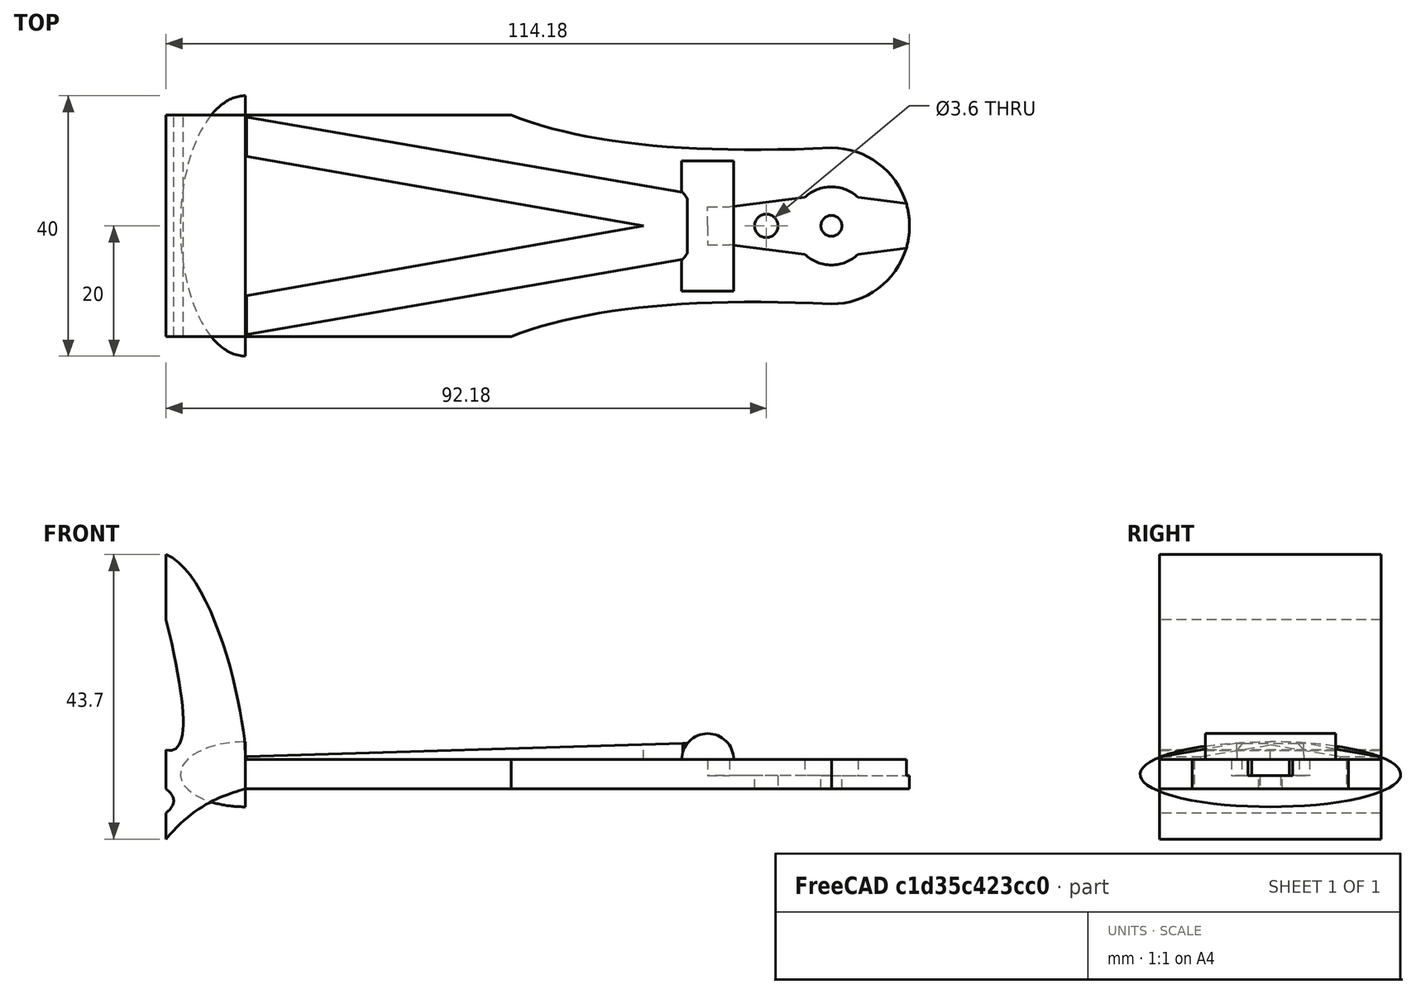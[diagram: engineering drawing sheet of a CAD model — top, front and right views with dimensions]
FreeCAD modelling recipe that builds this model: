
FCSTD DOCUMENT  (FreeCAD 0.18.4R)
Label: ServoCrawlerLeg
License: All rights reserved
LicenseURL: http://en.wikipedia.org/wiki/All_rights_reserved
objects: TechDraw::DrawViewDimension×8, Sketcher::SketchObject×7, TechDraw::DrawViewPart×7, Part::Extrusion×5, Part::MultiFuse×3, Part::Mirroring×2, Part::Cut×2, TechDraw::DrawSVGTemplate×2, TechDraw::DrawViewAnnotation×2, TechDraw::DrawPage×2, Spreadsheet::Sheet×1, Part::Fuse×1, Part::Ellipsoid×1, PartDesign::FeatureBase×1, PartDesign::Pad×1, PartDesign::Pocket×1, PartDesign::Body×1
note: 27 computed .brp shape members not serialized (recipe doc carries the construction recipe); baked Part::Feature solids carry a one-line shape summary decoded from their .brp

FEATURE [Sketcher::SketchObject] Sketch001
  sketch-geometry (15):
    g0: GeomPoint X=-90 Y=17 Z=0
    g1: LineSegment StartX=-90 StartY=17 StartZ=0 EndX=-49.2057 EndY=17 EndZ=0
    g2: Circle [constr] CenterX=0 CenterY=12 CenterZ=0 NormalX=0 NormalY=0 NormalZ=1 AngleXU=0 Radius=6
    g3: Circle [constr] CenterX=-49.2057 CenterY=17 CenterZ=0 NormalX=0 NormalY=0 NormalZ=1 AngleXU=0 Radius=6
    g4: ArcOfCircle CenterX=0 CenterY=0 CenterZ=0 NormalX=0 NormalY=0 NormalZ=1 AngleXU=0 Radius=12 StartAngle=0 EndAngle=1.5708
    g5: ArcOfCircle CenterX=0 CenterY=0 CenterZ=0 NormalX=0 NormalY=0 NormalZ=1 AngleXU=0 Radius=1.6 StartAngle=0 EndAngle=3.14159
    g6: LineSegment StartX=1.6 StartY=0 StartZ=0 EndX=12 EndY=0 EndZ=0
    g7: LineSegment StartX=-1.6 StartY=0 StartZ=0 EndX=-90 EndY=0 EndZ=0
    g8: Circle [constr] CenterX=0 CenterY=12 CenterZ=0 NormalX=0 NormalY=0 NormalZ=1 AngleXU=0 Radius=5
    g9: Circle [constr] CenterX=-32.5091 CenterY=10.4213 CenterZ=0 NormalX=0 NormalY=0 NormalZ=1 AngleXU=0 Radius=5
    g10: Circle [constr] CenterX=-49.2057 CenterY=17 CenterZ=0 NormalX=0 NormalY=0 NormalZ=1 AngleXU=0 Radius=5
    g11: BSplineCurve PolesCount=3 KnotsCount=2 Degree=2 IsPeriodic=0
    g12: GeomPoint [constr] X=0 Y=12 Z=0
    g13: GeomPoint [constr] X=-49.2057 Y=17 Z=0
    g14: LineSegment StartX=-90 StartY=0 StartZ=0 EndX=-90 EndY=17 EndZ=0
  constraints (28):
    c: DistanceX(g0,g2) = 90  'length'
    c: DistanceY(g2,g0) = 5
    c: Coincident(g1,g0)
    c: Horizontal(g1)
    c: Radius(g2) = 6
    c: Equal(g2,g3)
    c: Coincident(g3,g1)
    c: PointOnObject(g4,g-1)
    c: PointOnObject(g7,g-1)
    c: Coincident(g5,g-1)
    c: PointOnObject(g5,g-1)
    c: Coincident(g6,g5)
    c: Coincident(g6,g4)
    c: Horizontal(g6)
    c: Coincident(g7,g5)
    c: Radius(g5) = 1.6
    c: Radius(g8) = 5
    c: Equal(g8,g9)
    c: Equal(g8,g10)
    c: Coincident(g10,g1)
    c: InternalAlignment(g8,g11)
    c: InternalAlignment(g9,g11)
    c: InternalAlignment(g10,g11)
    c: InternalAlignment(g12,g11)
    c: InternalAlignment(g13,g11)
    c: Coincident(g14,g0)
    c: Coincident(g14,g7)
    c: Coincident(g8,g2)
FEATURE [Part::Extrusion] Extrude  label="arm"
  Base = -> Sketch001
  Dir = (0,0,1)
  DirMode = 2
  FaceMakerClass = Part::FaceMakerBullseye
  LengthFwd = 4.5
  LengthRev = 0
  Solid = true
  Symmetric = false
  expr: LengthFwd = global.height
FEATURE [Sketcher::SketchObject] Sketch008  label="servoHolderHole"
  AttachmentOffset = pos=(0,0,0) rot=(0,0,1;1.5708rad)
  MapMode = 5
  Placement = pos=(0,0,4.5) rot=(0,0,1;1.5708rad)
  Support = -> [Extrude]
  sketch-geometry (7):
    g0: GeomPoint X=0 Y=19 Z=0
    g1: LineSegment StartX=0 StartY=19 StartZ=0 EndX=2.9 EndY=19 EndZ=0
    g2: LineSegment StartX=2.9 StartY=19 StartZ=0 EndX=2.9 EndY=15.6827 EndZ=0
    g3: ArcOfCircle CenterX=0 CenterY=0 CenterZ=0 NormalX=0 NormalY=0 NormalZ=1 AngleXU=0 Radius=6 StartAngle=0 EndAngle=0.747584
    g4: LineSegment StartX=4.4 StartY=4.07922 StartZ=0 EndX=2.9 EndY=15.6827 EndZ=0
    g5: LineSegment StartX=0 StartY=0 StartZ=0 EndX=6 EndY=0 EndZ=0
    g6: LineSegment StartX=0 StartY=0 StartZ=0 EndX=0 EndY=19 EndZ=0
  constraints (18):
    c: PointOnObject(g0,g-2)
    c: DistanceY(g-1,g0) = 19  'servHoleL'
    c: Coincident(g1,g0)
    c: Horizontal(g1)
    c: DistanceX(g1,g1) = 2.9
    c: Coincident(g2,g1)
    c: Vertical(g2)
    c: Coincident(g3,g-1)
    c: Radius(g3) = 6
    c: PointOnObject(g3,g-1)
    c: DistanceX(g-1,g3) = 4.4
    c: Coincident(g4,g2)
    c: Distance(g4) = 11.7
    c: Coincident(g4,g3)
    c: Coincident(g5,g-1)
    c: Coincident(g5,g3)
    c: Coincident(g6,g-1)
    c: Coincident(g6,g0)
FEATURE [Spreadsheet::Sheet] Spreadsheet  label="global"
  cells = A1=height; B1(height)=4.5; A2=offsetBackwardServo; B2(offestSev)=-2.5
FEATURE [Part::Extrusion] Extrude004
  Base = -> Sketch008
  Dir = (0,0,1)
  DirMode = 2
  FaceMakerClass = Part::FaceMakerBullseye
  LengthFwd = 2.45
  LengthRev = 0
  Reversed = true
  Solid = true
  Symmetric = false
FEATURE [Part::Mirroring] Part__Mirroring002  label="Extrude004 (Mirror #3)"
  Base = (0,0,0)
  Normal = (1,0,0)
  Source = -> Extrude004
FEATURE [Part::MultiFuse] Fusion003
  Shapes = -> [Part__Mirroring002,Extrude004]
FEATURE [Part::Cut] Cut
  Base = -> Extrude
  Tool = -> Fusion003
FEATURE [Part::Mirroring] Part__Mirroring  label="Extrude (Mirror #1)"
  Base = (0,0,0)
  Normal = (0,1,0)
  Source = -> Cut
FEATURE [Sketcher::SketchObject] Sketch012
  MapMode = 5
  Placement = pos=(0,0,4) rot=(0,0,1;0rad)
  sketch-geometry (9):
    g0: LineSegment StartX=-89.8501 StartY=16.7026 StartZ=0 EndX=-22.8408 EndY=5.14242 EndZ=0
    g1: LineSegment StartX=-22.8408 StartY=-5.14242 StartZ=0 EndX=-89.8501 EndY=-16.7026 EndZ=0
    g2: LineSegment StartX=-89.8501 StartY=-16.7026 StartZ=0 EndX=-89.8501 EndY=-10.7026 EndZ=0
    g3: LineSegment StartX=-89.8501 StartY=-10.7026 StartZ=0 EndX=-28.8408 EndY=0 EndZ=0
    g4: LineSegment StartX=-28.8408 StartY=0 StartZ=0 EndX=-89.8501 EndY=10.7026 EndZ=0
    g5: LineSegment StartX=-89.8501 StartY=10.7026 StartZ=0 EndX=-89.8501 EndY=16.7026 EndZ=0
    g6: ArcOfCircle CenterX=-28.8408 CenterY=0 CenterZ=0 NormalX=0 NormalY=0 NormalZ=1 AngleXU=0 Radius=7.90218 StartAngle=5.5746 EndAngle=6.99177
    g7: LineSegment [constr] StartX=-89.8501 StartY=10.7026 StartZ=0 EndX=-89.8501 EndY=0 EndZ=0
    g8: LineSegment [constr] StartX=-89.8501 StartY=0 StartZ=0 EndX=-89.8501 EndY=-10.7026 EndZ=0
  constraints (22):
    c: Coincident(g2,g1)
    c: Vertical(g2)
    c: Coincident(g3,g2)
    c: PointOnObject(g3,g-1)
    c: Coincident(g4,g3)
    c: Coincident(g5,g4)
    c: Coincident(g5,g0)
    c: Vertical(g5)
    c: DistanceY(g2,g2) = 6
    c: DistanceY(g5,g5) = 6
    c: Coincident(g6,g3)
    c: Coincident(g6,g0)
    c: Coincident(g6,g1)
    c: DistanceX(g3,g0) = 6
    c: DistanceX(g3,g1) = 6
    c: Coincident(g7,g4)
    c: PointOnObject(g7,g-1)
    c: Coincident(g8,g7)
    c: Coincident(g8,g2)
    c: Vertical(g7)
    c: Vertical(g8)
    c: Equal(g7,g8)
FEATURE [Sketcher::SketchObject] Sketch013
  MapMode = 5
  Placement = pos=(0,0,0) rot=(1,0,0;1.5708rad)
  sketch-geometry (3):
    g0: LineSegment StartX=-90 StartY=5 StartZ=0 EndX=-22.1184 EndY=7 EndZ=0
    g1: LineSegment StartX=-22.1184 StartY=7 StartZ=0 EndX=-90 EndY=7 EndZ=0
    g2: LineSegment StartX=-90 StartY=7 StartZ=0 EndX=-90 EndY=5 EndZ=0
  constraints (8):
    c: Coincident(g1,g0)
    c: Horizontal(g1)
    c: Coincident(g2,g1)
    c: Coincident(g2,g0)
    c: Vertical(g2)
    c: DistanceX(g0,g-1) = 90
    c: DistanceY(g-1,g0) = 7
    c: DistanceY(g0,g1) = 2
FEATURE [Part::Extrusion] Extrude005
  Base = -> Sketch012
  Dir = (0,0,1)
  DirMode = 2
  FaceMakerClass = Part::FaceMakerBullseye
  LengthFwd = 3
  LengthRev = 0
  Solid = true
  Symmetric = false
FEATURE [Part::Extrusion] Extrude006
  Base = -> Sketch013
  Dir = (0,-1,0)
  DirMode = 2
  FaceMakerClass = Part::FaceMakerBullseye
  LengthFwd = 30
  LengthRev = 30
  Solid = true
  Symmetric = false
FEATURE [Part::Cut] Cut001  label="Strebe"
  Base = -> Extrude005
  Tool = -> Extrude006
FEATURE [Part::Fuse] Fusion
  Base = -> Cut
  Tool = -> Part__Mirroring
FEATURE [TechDraw::DrawSVGTemplate] Template
  EditableTexts = Designed_by_Name=Johannes Löwe; Drawing_number=0.0.1; FC-Date=24/03/2019; FC-SC=-; FC-SH=1; FC-Title=S.L.A.R Leg; Subtitle=Middle Component; Weight=19.5 g
  Height = 210
  Orientation = 1
  Width = 297
FEATURE [TechDraw::DrawViewPart] View  label="Top"
  Caption = Top
  CoarseView = true
  Direction = (0,0,1)
  Focus = 100
  HardHidden = false
  IsoCount = 0
  IsoHidden = false
  IsoVisible = true
  LockPosition = false
  Perspective = false
  Rotation = 0
  ScaleType = 1
  SeamHidden = false
  SeamVisible = false
  SmoothHidden = false
  SmoothVisible = true
  X = 133.52
  Y = 56.71
FEATURE [TechDraw::DrawViewPart] View001  label="Front"
  Caption = Front
  CoarseView = true
  Direction = (0,1,0)
  Focus = 100
  HardHidden = false
  IsoCount = 0
  IsoHidden = false
  IsoVisible = false
  LockPosition = false
  Perspective = true
  Rotation = 0
  ScaleType = 0
  SeamHidden = false
  SeamVisible = false
  SmoothHidden = false
  SmoothVisible = false
  X = 216.314
  Y = 87.8478
FEATURE [TechDraw::DrawViewPart] View002  label="Perspective"
  Caption = The S.L.A.R. Leg
  CoarseView = true
  Direction = (-0.2,1,1)
  Focus = 200
  HardHidden = false
  IsoCount = 0
  IsoHidden = false
  IsoVisible = true
  LockPosition = false
  Perspective = false
  Rotation = 0
  Scale = 1.5
  ScaleType = 0
  SeamHidden = false
  SeamVisible = false
  SmoothHidden = true
  SmoothVisible = false
  X = 69.0301
  Y = 169.689
  expr: Direction.x = -0.2
FEATURE [TechDraw::DrawViewDimension] Dimension
  Arbitrary = false
  FormatSpec = %.2f
  LockPosition = false
  MeasureType = 1
  OverTolerance = 0
  References2D = -> [View]
  Rotation = 0
  ScaleType = 0
  Type = 2
  UnderTolerance = 0
  X = -113.183
  Y = -28.0041
FEATURE [TechDraw::DrawViewDimension] Dimension001
  Arbitrary = false
  FormatSpec = %.2f
  LockPosition = false
  MeasureType = 1
  OverTolerance = 0
  References2D = -> [View001]
  Rotation = 0
  ScaleType = 0
  Type = 1
  UnderTolerance = 0
  X = 31.1719
  Y = 20.5356
FEATURE [TechDraw::DrawViewDimension] Dimension002
  Arbitrary = false
  FormatSpec = %.2f
  LockPosition = false
  MeasureType = 1
  OverTolerance = 0
  References2D = -> [View]
  Rotation = 0
  ScaleType = 0
  Type = 2
  UnderTolerance = 0
  X = -69.0862
  Y = -0.822454
FEATURE [TechDraw::DrawViewDimension] Dimension003
  Arbitrary = false
  FormatSpec = %.2f
  LockPosition = false
  MeasureType = 1
  OverTolerance = 0
  References2D = -> [View]
  Rotation = 0
  ScaleType = 0
  Type = 2
  UnderTolerance = 0
  X = -91.294
  Y = -1.64851
FEATURE [TechDraw::DrawViewDimension] Dimension004
  Arbitrary = false
  FormatSpec = %.2f
  LockPosition = false
  MeasureType = 1
  OverTolerance = 0
  References2D = -> [View002]
  Rotation = 0
  ScaleType = 0
  Type = 0
  UnderTolerance = 0
  X = 1.50159
  Y = -39.0413
FEATURE [TechDraw::DrawViewAnnotation] Annotation
  Font = osifont
  LineSpace = 80
  LockPosition = false
  MaxWidth = -1
  Rotation = 0
  ScaleType = 0
  Text = Radboud University
  TextSize = 5
  TextStyle = 2
  X = 214.014
  Y = 35.8125
FEATURE [TechDraw::DrawPage] Page
  KeepUpdated = true
  ProjectionType = 0
  Template = -> Template
  Views = -> [View,View001,View002,Dimension,Dimension001,Dimension002,Dimension003,Dimension004,Annotation]
FEATURE [Part::MultiFuse] Fusion004
  Shapes = -> [Cut001,Fusion]
FEATURE [Sketcher::SketchObject] Sketch015  label="HoleServoScrew2"
  MapMode = 5
  Placement = pos=(0,0,4) rot=(0,0,1;0rad)
  sketch-geometry (1):
    g0: Circle CenterX=-10 CenterY=0 CenterZ=0 NormalX=0 NormalY=0 NormalZ=1 AngleXU=0 Radius=1.8
  constraints (3):
    c: PointOnObject(g0,g-1)
    c: DistanceX(g0,g-1) = 10
    c: Radius(g0) = 1.8
FEATURE [Part::Ellipsoid] Ellipsoid
  Angle1 = -90
  Angle2 = 90
  Angle3 = 180
  AttacherType = Attacher::AttachEngine3D
  Placement = pos=(-90,0,2.25) rot=(0,0,1;1.5708rad)
  Radius1 = 5
  Radius2 = 20
  Radius3 = 10
  expr: Placement.Base.z = global.height / 2
  expr: Placement.Base.x = -1 * Sketch001.Constraints.length
FEATURE [Sketcher::SketchObject] Sketch  label="shoe"
  Placement = pos=(0,0,0) rot=(1,0,0;1.5708rad)
  expr: Constraints[4] = arm.LengthFwd
  expr: Constraints[6] = servoHolderHole.Constraints.servHoleL
  sketch-geometry (2):
    g0: ArcOfCircle CenterX=-19 CenterY=4.5 CenterZ=0 NormalX=0 NormalY=0 NormalZ=1 AngleXU=0 Radius=4 StartAngle=0 EndAngle=3.14159
    g1: LineSegment StartX=-23 StartY=4.5 StartZ=0 EndX=-15 EndY=4.5 EndZ=0
  constraints (7):
    c: Radius(g0) = 4
    c: Coincident(g1,g0)
    c: Coincident(g1,g0)
    c: Horizontal(g1)
    c: DistanceY(g-1,g0) = 4.5
    c: PointOnObject(g0,g1)
    c: DistanceX(g0,g-1) = 19
FEATURE [Sketcher::SketchObject] Sketch016  label="Foot"
  Placement = pos=(0,0,0) rot=(1,0,0;1.5708rad)
  sketch-geometry (32):
    g0-g3: Circle [constr] x4 (B-spline internal-alignment scaffolding for g4; pole/knot coordinates omitted)
    g4: BSplineCurve PolesCount=4 KnotsCount=2 Degree=3 IsPeriodic=0
    g5: GeomPoint [constr] X=-90 Y=0 Z=0
    g6: GeomPoint [constr] X=-102.176 Y=-7.69826 Z=0
    g7: LineSegment StartX=-102.176 StartY=-7.69826 StartZ=0 EndX=-102.176 EndY=-3.69826 EndZ=0
    g8: Circle [constr] CenterX=-102.176 CenterY=-3.69826 CenterZ=0 NormalX=0 NormalY=0 NormalZ=1 AngleXU=0 Radius=0.9
    g9: Circle [constr] CenterX=-99.8759 CenterY=-1.76634 CenterZ=0 NormalX=0 NormalY=0 NormalZ=1 AngleXU=0 Radius=0.9
    g10: Circle [constr] CenterX=-102.176 CenterY=0 CenterZ=0 NormalX=0 NormalY=0 NormalZ=1 AngleXU=0 Radius=0.9
    g11: BSplineCurve PolesCount=3 KnotsCount=2 Degree=2 IsPeriodic=0
    g12: GeomPoint [constr] X=-102.176 Y=-3.69826 Z=0
    g13: GeomPoint [constr] X=-102.176 Y=0 Z=0
    g14: LineSegment StartX=-102.176 StartY=0 StartZ=0 EndX=-102.176 EndY=6 EndZ=0
    g15: Circle [constr] CenterX=-102.176 CenterY=6 CenterZ=0 NormalX=0 NormalY=0 NormalZ=1 AngleXU=0 Radius=0.8
    g16: Circle [constr] CenterX=-96.9441 CenterY=4.63827 CenterZ=0 NormalX=0 NormalY=0 NormalZ=1 AngleXU=0 Radius=0.8
    g17: Circle [constr] CenterX=-102.176 CenterY=26 CenterZ=0 NormalX=0 NormalY=0 NormalZ=1 AngleXU=0 Radius=0.8
    g18: BSplineCurve PolesCount=3 KnotsCount=2 Degree=2 IsPeriodic=0
    g19: GeomPoint [constr] X=-102.176 Y=6 Z=0
    g20: GeomPoint [constr] X=-102.176 Y=26 Z=0
    g21: LineSegment StartX=-102.176 StartY=26 StartZ=0 EndX=-102.176 EndY=36 EndZ=0
    g22-g25: Circle [constr] x4 (B-spline internal-alignment scaffolding for g26; pole/knot coordinates omitted)
    g26: BSplineCurve PolesCount=4 KnotsCount=2 Degree=3 IsPeriodic=0
    g27: GeomPoint [constr] X=-102.176 Y=36 Z=0
    g28: GeomPoint [constr] X=-90 Y=4.39385 Z=0
    g29: LineSegment StartX=-90 StartY=4.39385 StartZ=0 EndX=-90 EndY=0 EndZ=0
    g30: LineSegment [constr] StartX=-102.176 StartY=26 StartZ=0 EndX=-102.176 EndY=6 EndZ=0
    g31: LineSegment [constr] StartX=-102.176 StartY=0 StartZ=0 EndX=-102.176 EndY=-3.69826 EndZ=0
  constraints (54):
    c: PointOnObject(g4,g-1)
    c: Equal(g0,g1)
    c: Equal(g0,g2)
    c: Equal(g0,g3)
    c: InternalAlignment(g0-g3 -> g4) x4
    c: InternalAlignment(g5,g4)
    c: InternalAlignment(g6,g4)
    c: DistanceX(g4,g-1) = 90
    c: Coincident(g11,g7)
    c: Radius(g8) = 0.9
    c: Equal(g8,g9)
    c: Equal(g8,g10)
    c: PointOnObject(g11,g-1)
    c: InternalAlignment(g8,g11)
    c: InternalAlignment(g9,g11)
    c: InternalAlignment(g10,g11)
    c: InternalAlignment(g12,g11)
    c: InternalAlignment(g13,g11)
    c: Coincident(g14,g11)
    c: Vertical(g14)
    c: Coincident(g18,g14)
    c: Radius(g15) = 0.8
    c: Equal(g15,g16)
    c: Equal(g15,g17)
    c: InternalAlignment(g15,g18)
    c: InternalAlignment(g16,g18)
    c: InternalAlignment(g17,g18)
    c: InternalAlignment(g19,g18)
    c: InternalAlignment(g20,g18)
    c: Coincident(g21,g18)
    c: Coincident(g26,g21)
    c: Radius(g22) = 0.7
    c: Equal(g22,g23)
    c: Equal(g22,g24)
    c: Equal(g22,g25)
    c: InternalAlignment(g22-g25 -> g26) x4
    c: InternalAlignment(g27,g26)
    c: InternalAlignment(g28,g26)
    c: Coincident(g29,g26)
    c: Coincident(g29,g4)
    c: Vertical(g29)
    c: Vertical(g21)
    c: Coincident(g7,g4)
    c: Vertical(g7)
    c: Coincident(g30,g18)
    c: Coincident(g30,g14)
    c: Coincident(g31,g11)
    c: Coincident(g31,g7)
    c: Vertical(g31)
    c: Vertical(g30)
    c: DistanceY(g30,g30) = 20
    c: DistanceY(g21,g21) = 10
    c: DistanceY(g14,g14) = 6
    c: DistanceY(g7,g7) = 4
FEATURE [Part::Extrusion] Extrude007  label="FootE"
  Base = -> Sketch016
  Dir = (0,-1,0)
  DirMode = 2
  FaceMakerClass = Part::FaceMakerBullseye
  LengthFwd = 17
  LengthRev = 17
  Solid = true
  Symmetric = false
FEATURE [Part::MultiFuse] Fusion005
  Shapes = -> [Extrude007,Fusion004]
FEATURE [PartDesign::FeatureBase] BaseFeature
  BaseFeature = -> Fusion005
FEATURE [PartDesign::Pad] Pad
  BaseFeature = -> BaseFeature
  Length = 10
  Length2 = 10
  Profile = -> Sketch
  Reversed = true
  Type = 4
FEATURE [PartDesign::Pocket] Pocket
  BaseFeature = -> Pad
  Length = 28
  Length2 = 100
  Midplane = true
  Profile = -> Sketch015
  Type = 0
FEATURE [PartDesign::Body] Body
  BaseFeature = -> Fusion005
  Group = -> [BaseFeature,Sketch015,Sketch,Pad,Pocket]
  Origin = -> Origin
  Tip = -> Pocket
FEATURE [TechDraw::DrawSVGTemplate] Template001
  EditableTexts = Designed_by_Name=Johannes Loewe; Drawing_number=0.0.1; FC-Date=Date; FC-SC=1; FC-SH=1; FC-Title=RWML Crawler; Subtitle=Secondary Leg; Weight=20g
  Height = 210
  Orientation = 1
  Width = 297
FEATURE [TechDraw::DrawViewPart] View003  label=" Front"
  CoarseView = false
  Direction = (0.03,-0.72,0)
  Focus = 100
  HardHidden = false
  IsoCount = 0
  IsoHidden = false
  IsoVisible = false
  LockPosition = false
  Perspective = false
  Rotation = 0
  ScaleType = 0
  SeamHidden = false
  SeamVisible = false
  SmoothHidden = false
  SmoothVisible = false
  Source = -> [Fusion005]
  X = 77.0211
  Y = 172.962
FEATURE [TechDraw::DrawViewPart] View004  label=" Top"
  CoarseView = false
  Direction = (0.03,0,0.69)
  Focus = 100
  HardHidden = false
  IsoCount = 0
  IsoHidden = false
  IsoVisible = false
  LockPosition = false
  Perspective = false
  Rotation = 0
  ScaleType = 0
  SeamHidden = false
  SeamVisible = false
  SmoothHidden = false
  SmoothVisible = false
  Source = -> [Fusion005]
  X = 37.3235
  Y = 79.7899
FEATURE [TechDraw::DrawViewPart] View005
  CoarseView = false
  Direction = (0.029,-0.723,0.691)
  Focus = 100
  HardHidden = false
  IsoCount = 0
  IsoHidden = false
  IsoVisible = false
  LockPosition = false
  Perspective = false
  Rotation = 0
  ScaleType = 0
  SeamHidden = false
  SeamVisible = false
  SmoothHidden = false
  SmoothVisible = false
  Source = -> [Fusion005]
  X = 210.503
  Y = 165.604
FEATURE [TechDraw::DrawViewPart] View006
  CoarseView = false
  Direction = (-0.5,-0.7,0.69)
  Focus = 100
  HardHidden = false
  IsoCount = 0
  IsoHidden = false
  IsoVisible = false
  LockPosition = false
  Perspective = false
  Rotation = 0
  ScaleType = 0
  SeamHidden = false
  SeamVisible = false
  SmoothHidden = false
  SmoothVisible = false
  Source = -> [Fusion005]
  X = 194.937
  Y = 107.118
FEATURE [TechDraw::DrawViewDimension] Dimension005
  Arbitrary = false
  FormatSpec = %.2f
  LockPosition = false
  MeasureType = 1
  OverTolerance = 0
  References2D = -> [View003]
  Rotation = 0
  ScaleType = 0
  Type = 1
  UnderTolerance = 0
  X = 1.11318
  Y = -20.2689
FEATURE [TechDraw::DrawViewDimension] Dimension006
  Arbitrary = false
  FormatSpec = %.2f
  LockPosition = false
  MeasureType = 1
  OverTolerance = 0
  References2D = -> [View004]
  Rotation = 0
  ScaleType = 0
  Type = 2
  UnderTolerance = 0
  X = 22.3081
  Y = -1.65698
FEATURE [TechDraw::DrawViewDimension] Dimension007
  Arbitrary = false
  FormatSpec = %.2f
  LockPosition = false
  MeasureType = 1
  OverTolerance = 0
  References2D = -> [View004]
  Rotation = 0
  ScaleType = 0
  Type = 1
  UnderTolerance = 0
  X = -1.10465
  Y = 53.1211
FEATURE [TechDraw::DrawViewAnnotation] Annotation001
  Font = DejaVu Sans
  LineSpace = 80
  LockPosition = false
  MaxWidth = -1
  Rotation = 0
  ScaleType = 0
  Text = NUI Galway
  TextSize = 6
  TextStyle = 2
  X = 209.307
  Y = 35.4202
FEATURE [TechDraw::DrawPage] Page001
  KeepUpdated = true
  ProjectionType = 0
  Template = -> Template001
  Views = -> [View003,View004,View005,View006,Dimension005,Dimension006,Dimension007,Annotation001]
